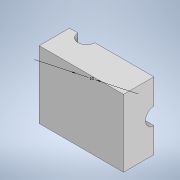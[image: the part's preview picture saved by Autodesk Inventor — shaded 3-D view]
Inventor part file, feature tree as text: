
AUTODESK INVENTOR PART (.ipt)
format: ipt  version: 2022 (Build 260153000, 153)  size: 135,680 bytes
history: native  units: mm
features: sketch x3, extrude x3, split x1, boolean_combine x1, fillet x1
ambient origin geometry x8: Origin, YZ Plane, XZ Plane, XY Plane, X Axis, Y Axis, Z Axis, Center Point
bodies: Solid1 (feature_tree), Solid2 (feature_tree)
feature tree (9):
  sketch  "Sketch1"  dims[d0=10.0mm d1=40.0mm d2=0.0mm]
  extrude  "Extrusion1"  Depth=40.0mm TaperAngle=0.0deg
  extrude  "Extrusion2"  Depth=40.0mm TaperAngle=0.0deg
  split  "Split1"
  extrude  "Extrusion3"  Depth=40.0mm
  boolean_combine  "Combine1"
  fillet  "Fillet1"  Radius=18.0mm
  sketch  "Sketch2"  dims[d3=10.0mm d4=40.0mm d5=0.0mm]
  sketch  "Sketch3"  dims[d6=50.0mm d7=40.0mm d8=18.0mm d9=0.0mm d10=10.0mm]
